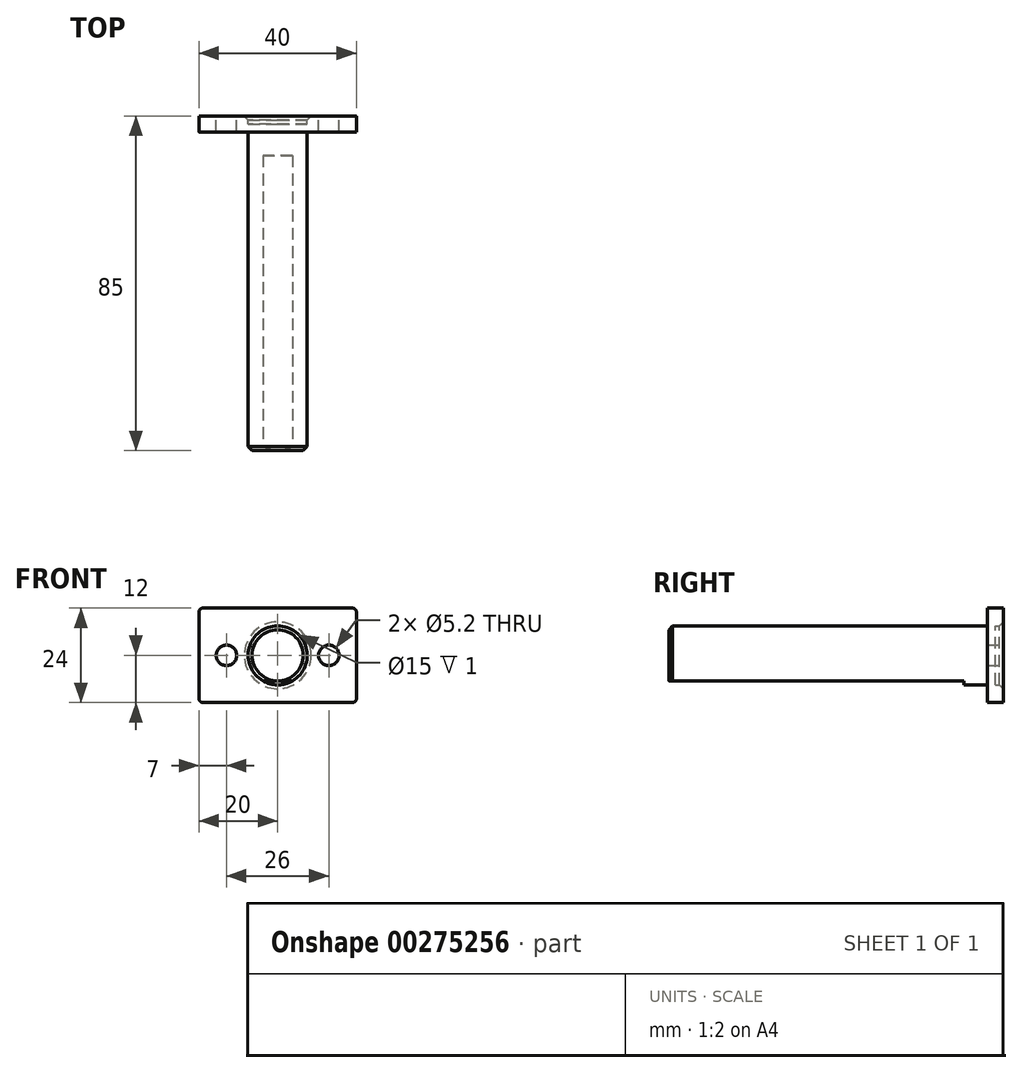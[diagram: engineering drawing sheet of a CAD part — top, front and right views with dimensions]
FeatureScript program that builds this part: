
annotation { "Feature Type Name" : "Feature", "Feature Type Description" : "" }
export const myFeature = defineFeature(function(context is Context, id is Id, definition is map)
    precondition{}
    {
        {
            var Q0;
            Q0=qCreatedBy(makeId("Front.planeOp"),FACE);
            var sketch = newSketch(context, id + "F0", { "sketchPlane" : qUnion([Q0])});
            skLineSegment(sketch, "E0.bottom", {"start": v(20, -12) * mm, "end": v(-20, -12) * mm});
            skLineSegment(sketch, "E0.top", {"start": v(20, 12) * mm, "end": v(-20, 12) * mm});
            skLineSegment(sketch, "E0.left", {"start": v(20, -12) * mm, "end": v(20, 12) * mm});
            skLineSegment(sketch, "E0.right", {"start": v(-20, -12) * mm, "end": v(-20, 12) * mm});
            skPoint(sketch, "E0.middle", {"position": v(0, 0) * mm});
            skPoint(sketch, "E1", {"position": v(-13, 0) * mm});
            skPoint(sketch, "E2", {"position": v(13, 0) * mm});
            skCircle(sketch, "E3", {"center": v(0, 0) * mm, "radius": 7.5 * mm});
            skSolve(sketch);
        }
        {
            var Q0;
            Q0=makeQuery(id+"F0.imprint","IMPRINT",FACE,{"disambiguationData":[TD([[makeQuery(id+"F0.imprint","IMPRINT",EDGE,{"derivedFrom":sQuery(id+"F0.wireOp",EDGE,"E0.bottom")}),-1.0]])]});
            extrude(context, id + "F1", {"entities" : qUnion([Q0]), "endBound" : BoundingType.SYMMETRIC, "depth" : 4 * mm});
        }
        {
            var Q0;
            Q0=makeQuery(id+"F0.imprint","IMPRINT",FACE,{"disambiguationData":[TD([[makeQuery(id+"F0.imprint","IMPRINT",EDGE,{"derivedFrom":sQuery(id+"F0.wireOp",EDGE,"E3")}),1.0]])]});
            extrude(context, id + "F2", {"entities" : qUnion([Q0]), "operationType" : NewBodyOperationType.ADD, "depth" : 83 * mm});
        }
        {
            var Q0;
            Q0=makeQuery(id+"F1.opExtrude","CAP_FACE",FACE,{"disambiguationData":[OSD([sQuery(id+"F0.wireOp",EDGE,"E0.bottom"),sQuery(id+"F0.wireOp",EDGE,"E0.top"),sQuery(id+"F0.wireOp",EDGE,"E0.left"),sQuery(id+"F0.wireOp",EDGE,"E0.right"),sQuery(id+"F0.wireOp",EDGE,"E3")])],"isStart":true});
            var sketch = newSketch(context, id + "F3", { "sketchPlane" : qUnion([Q0])});
            skPoint(sketch, "E4.0", {"position": v(-13, 0) * mm});
            skPoint(sketch, "E5.0", {"position": v(13, 0) * mm});
            skSolve(sketch);
        }
        {
            var Q0;
            Q0=sQuery(id+"F3.wireOp",VERTEX,"E4.0");
            var Q1;
            Q1=sQuery(id+"F3.wireOp",VERTEX,"E5.0");
            var Q2;
            Q2=makeQuery(id+"F1.opExtrude","SWEPT_BODY",BODY,{"disambiguationData":[OSD([sQuery(id+"F0.wireOp",EDGE,"E0.bottom"),sQuery(id+"F0.wireOp",EDGE,"E0.top"),sQuery(id+"F0.wireOp",EDGE,"E0.left"),sQuery(id+"F0.wireOp",EDGE,"E0.right"),sQuery(id+"F0.wireOp",EDGE,"E3")])]});
            hole(context, id + "F4", {"style" : HoleStyle.SIMPLE, "endStyle" : HoleEndStyle.BLIND, "holeDiameter" : 5.2 * mm, "holeDepth" : 15 * mm, "tappedDepth" : 12 * mm, "tapClearance" : 3, "startFromSketch" : true, "locations" : qUnion([Q0, Q1]), "scope" : qUnion([Q2])});
        }
        {
            var Q0;
            Q0=qCreatedBy(makeId("Front.planeOp"),FACE);
            var sketch = newSketch(context, id + "F5", { "sketchPlane" : qUnion([Q0])});
            skArc(sketch, "E6.0", {"start": v(-3.74, -6.5) * mm, "mid": v(0, -7.5) * mm, "end": v(3.74, -6.5) * mm});
            skPoint(sketch, "E7", {"position": v(0, -7.5) * mm});
            skLineSegment(sketch, "E8", {"start": v(0, -7.5) * mm, "end": v(0, -6.5) * mm, "construction": true});
            skLineSegment(sketch, "E9", {"start": v(3.74, -6.5) * mm, "end": v(-3.74, -6.5) * mm});
            skSolve(sketch);
        }
        {
            var Q0;
            Q0 = qSketchRegion(id + "F5", true);
            extrude(context, id + "F6", {"entities" : qUnion([Q0]), "operationType" : NewBodyOperationType.REMOVE, "oppositeDirection" : true, "depth" : 75 * mm});
        }
        {
            var Q0;
            Q0=makeQuery(id+"F2.opExtrude","CAP_FACE",FACE,{"disambiguationData":[OSD([sQuery(id+"F0.wireOp",EDGE,"E3")])],"isStart":false});
            var sketch = newSketch(context, id + "F7", { "sketchPlane" : qUnion([Q0])});
            skLineSegment(sketch, "E10.0", {"start": v(3.74, -6.5) * mm, "end": v(-3.74, -6.5) * mm});
            skArc(sketch, "E11.0", {"start": v(-3.74, -6.5) * mm, "mid": v(0, -7.5) * mm, "end": v(3.74, -6.5) * mm});
            skSolve(sketch);
        }
        {
            var Q0;
            Q0=makeQuery(id+"F7.imprint","IMPRINT",FACE,{"disambiguationData":[TD([[makeQuery(id+"F7.imprint","IMPRINT",EDGE,{"derivedFrom":sQuery(id+"F7.wireOp",EDGE,"E10.0")}),1.0]])]});
            extrude(context, id + "F8", {"entities" : qUnion([Q0]), "operationType" : NewBodyOperationType.REMOVE, "oppositeDirection" : true, "depth" : 75 * mm});
        }
        {
            var Q0;
            Q0=makeQuery(id+"F1.opExtrude","CAP_EDGE",EDGE,{"disambiguationData":[OSD([sQuery(id+"F0.wireOp",EDGE,"E3")])],"isStart":true});
            var Q1;
            Q1=makeQuery(id+"F2.opExtrude","CAP_EDGE",EDGE,{"disambiguationData":[OSD([sQuery(id+"F0.wireOp",EDGE,"E3")])],"isStart":false});
            chamfer(context, id + "F9", {"entities" : qUnion([Q0, Q1]), "width" : 1 * mm, "tangentPropagation" : true});
        }
        {
            var Q0;
            Q0=makeQuery(id+"F1.opExtrude","SWEPT_EDGE",EDGE,{"disambiguationData":[OSD([sQuery(id+"F0.wireOp",EDGE,"E0.top"),sQuery(id+"F0.wireOp",EDGE,"E0.left")])]});
            var Q1;
            Q1=makeQuery(id+"F1.opExtrude","SWEPT_EDGE",EDGE,{"disambiguationData":[OSD([sQuery(id+"F0.wireOp",EDGE,"E0.top"),sQuery(id+"F0.wireOp",EDGE,"E0.right")])]});
            var Q2;
            Q2=makeQuery(id+"F1.opExtrude","SWEPT_EDGE",EDGE,{"disambiguationData":[OSD([sQuery(id+"F0.wireOp",EDGE,"E0.bottom"),sQuery(id+"F0.wireOp",EDGE,"E0.left")])]});
            var Q3;
            Q3=makeQuery(id+"F1.opExtrude","SWEPT_EDGE",EDGE,{"disambiguationData":[OSD([sQuery(id+"F0.wireOp",EDGE,"E0.bottom"),sQuery(id+"F0.wireOp",EDGE,"E0.right")])]});
            fillet(context, id + "F10", {"entities" : qUnion([Q0, Q1, Q2, Q3]), "radius" : 1 * mm, "tangentPropagation" : true, "allowEdgeOverflow" : false});
        }
    });
